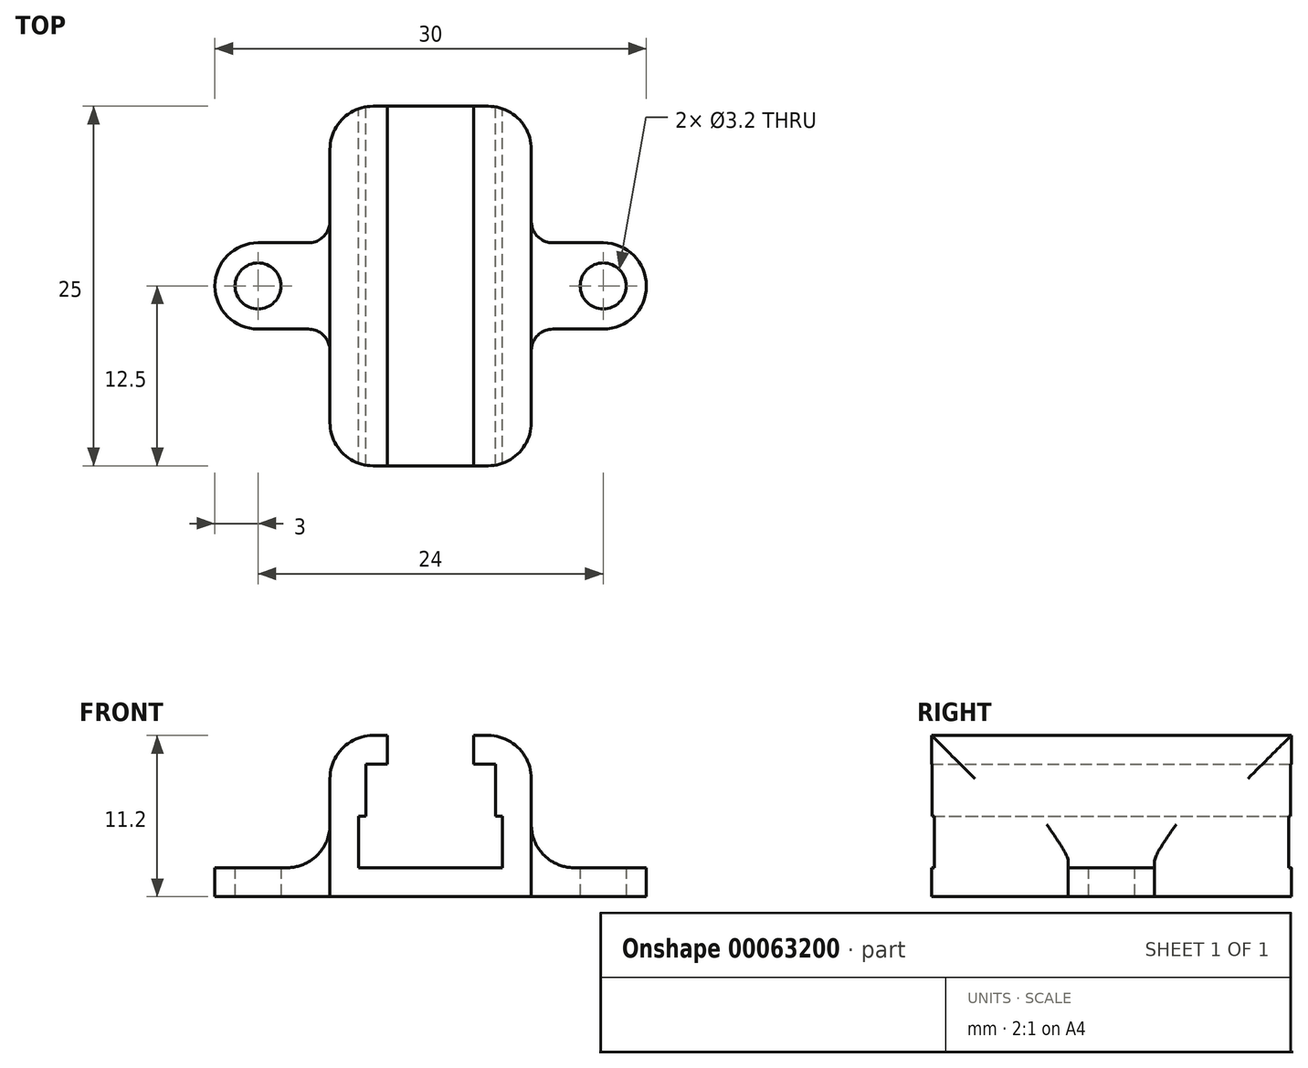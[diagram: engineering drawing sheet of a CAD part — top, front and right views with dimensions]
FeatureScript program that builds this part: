
annotation { "Feature Type Name" : "Feature", "Feature Type Description" : "" }
export const myFeature = defineFeature(function(context is Context, id is Id, definition is map)
    precondition{}
    {
        {
            var Q0;
            Q0=qCreatedBy(makeId("Front.planeOp"),FACE);
            var sketch = newSketch(context, id + "F0", { "sketchPlane" : qUnion([Q0])});
            skLineSegment(sketch, "E0", {"start": v(0, 0) * mm, "end": v(7, 0) * mm});
            skLineSegment(sketch, "E1", {"start": v(7, 0) * mm, "end": v(7, 11.2) * mm});
            skLineSegment(sketch, "E2", {"start": v(7, 11.2) * mm, "end": v(3, 11.2) * mm});
            skLineSegment(sketch, "E3", {"start": v(3, 11.2) * mm, "end": v(3, 9.2) * mm});
            skLineSegment(sketch, "E4", {"start": v(3, 9.2) * mm, "end": v(4.5, 9.2) * mm});
            skLineSegment(sketch, "E5", {"start": v(4.5, 9.2) * mm, "end": v(4.5, 5.6) * mm});
            skLineSegment(sketch, "E6", {"start": v(4.5, 5.6) * mm, "end": v(5, 5.6) * mm});
            skLineSegment(sketch, "E7", {"start": v(5, 5.6) * mm, "end": v(5, 2) * mm});
            skLineSegment(sketch, "E8", {"start": v(5, 2) * mm, "end": v(0, 2) * mm});
            skLineSegment(sketch, "E9", {"start": v(0, 2) * mm, "end": v(0, 0) * mm});
            skSolve(sketch);
        }
        {
            var Q0;
            Q0 = qSketchRegion(id + "F0", true);
            extrude(context, id + "F1", {"entities" : qUnion([Q0]), "depth" : 25 * mm});
        }
        {
            var Q0;
            Q0=qCreatedBy(makeId("Top.planeOp"),FACE);
            var sketch = newSketch(context, id + "F2", { "sketchPlane" : qUnion([Q0])});
            skLineSegment(sketch, "E10", {"start": v(0, 0) * mm, "end": v(0, -25) * mm, "construction": true});
            skLineSegment(sketch, "E11.bottom", {"start": v(8.5, -9.5) * mm, "end": v(15, -9.5) * mm});
            skLineSegment(sketch, "E11.top", {"start": v(8.5, -15.5) * mm, "end": v(15, -15.5) * mm});
            skLineSegment(sketch, "E11.left", {"start": v(0, -9.5) * mm, "end": v(0, -15.5) * mm});
            skLineSegment(sketch, "E11.right", {"start": v(15, -9.5) * mm, "end": v(15, -15.5) * mm});
            skLineSegment(sketch, "E12", {"start": v(15, -12.5) * mm, "end": v(0, -12.5) * mm, "construction": true});
            skCircle(sketch, "E13", {"center": v(12, -12.5) * mm, "radius": 1.6 * mm});
            skCircle(sketch, "E14", {"center": v(8.5, -8) * mm, "radius": 1.5 * mm, "construction": true});
            skLineSegment(sketch, "E15", {"start": v(8.5, -8) * mm, "end": v(8.5, -9.5) * mm, "construction": true});
            skLineSegment(sketch, "E16", {"start": v(8.5, -8) * mm, "end": v(7, -8) * mm, "construction": true});
            skArc(sketch, "E17", {"start": v(7, -8) * mm, "mid": v(7.44, -9.06) * mm, "end": v(8.5, -9.5) * mm});
            skLineSegment(sketch, "E18", {"start": v(7, -8) * mm, "end": v(0, -8) * mm});
            skLineSegment(sketch, "E19", {"start": v(0, -8) * mm, "end": v(0, -9.5) * mm});
            skLineSegment(sketch, "E20.MirrorCS", {"start": v(0, -17) * mm, "end": v(0, -15.5) * mm});
            skLineSegment(sketch, "E21.MirrorCS", {"start": v(7, -17) * mm, "end": v(0, -17) * mm});
            skArc(sketch, "E22.MirrorCS", {"start": v(7, -17) * mm, "mid": v(7.44, -15.94) * mm, "end": v(8.5, -15.5) * mm});
            skSolve(sketch);
        }
        {
            var Q0;
            Q0 = qSketchRegion(id + "F2", true);
            extrude(context, id + "F3", {"entities" : qUnion([Q0]), "operationType" : NewBodyOperationType.ADD, "depth" : 2 * mm});
        }
        {
            var Q0;
            Q0=makeQuery(id+"F3.boolean.opBoolean","INTERSECT",EDGE,{"derivedFrom":[makeQuery(id+"F1.opExtrude","SWEPT_FACE",FACE,{"disambiguationData":[OSD([sQuery(id+"F0.wireOp",EDGE,"E1")])]}),makeQuery(id+"F3.opExtrude","CAP_FACE",FACE,{"disambiguationData":[OSD([sQuery(id+"F2.wireOp",EDGE,"E11.bottom"),sQuery(id+"F2.wireOp",EDGE,"E11.top"),sQuery(id+"F2.wireOp",EDGE,"E11.left"),sQuery(id+"F2.wireOp",EDGE,"E11.right"),sQuery(id+"F2.wireOp",EDGE,"E13"),sQuery(id+"F2.wireOp",EDGE,"E17"),sQuery(id+"F2.wireOp",EDGE,"E18"),sQuery(id+"F2.wireOp",EDGE,"E19"),sQuery(id+"F2.wireOp",EDGE,"E20.MirrorCS"),sQuery(id+"F2.wireOp",EDGE,"E21.MirrorCS"),sQuery(id+"F2.wireOp",EDGE,"E22.MirrorCS")])],"isStart":false})]});
            var Q1;
            Q1=makeQuery(id+"F3.opExtrude","SWEPT_EDGE",EDGE,{"disambiguationData":[OSD([sQuery(id+"F2.wireOp",EDGE,"E11.top"),sQuery(id+"F2.wireOp",EDGE,"E11.right")])]});
            var Q2;
            Q2=makeQuery(id+"F3.opExtrude","SWEPT_EDGE",EDGE,{"disambiguationData":[OSD([sQuery(id+"F2.wireOp",EDGE,"E11.bottom"),sQuery(id+"F2.wireOp",EDGE,"E11.right")])]});
            var Q3;
            Q3=makeQuery(id+"F1.opExtrude","CAP_EDGE",EDGE,{"disambiguationData":[OSD([sQuery(id+"F0.wireOp",EDGE,"E1")])],"isStart":false});
            var Q4;
            Q4=makeQuery(id+"F1.opExtrude","CAP_EDGE",EDGE,{"disambiguationData":[OSD([sQuery(id+"F0.wireOp",EDGE,"E1")])],"isStart":true});
            var Q5;
            Q5=makeQuery(id+"F1.opExtrude","SWEPT_EDGE",EDGE,{"disambiguationData":[OSD([sQuery(id+"F0.wireOp",EDGE,"E1"),sQuery(id+"F0.wireOp",EDGE,"E2")])]});
            fillet(context, id + "F4", {"entities" : qUnion([Q0, Q1, Q2, Q3, Q4, Q5]), "radius" : 3 * mm, "tangentPropagation" : true, "allowEdgeOverflow" : false});
        }
        {
            var Q0;
            Q0=makeQuery(id+"F1.opExtrude","SWEPT_BODY",BODY,{"disambiguationData":[OSD([sQuery(id+"F0.wireOp",EDGE,"E0"),sQuery(id+"F0.wireOp",EDGE,"E1"),sQuery(id+"F0.wireOp",EDGE,"E2"),sQuery(id+"F0.wireOp",EDGE,"E3"),sQuery(id+"F0.wireOp",EDGE,"E4"),sQuery(id+"F0.wireOp",EDGE,"E5"),sQuery(id+"F0.wireOp",EDGE,"E6"),sQuery(id+"F0.wireOp",EDGE,"E7"),sQuery(id+"F0.wireOp",EDGE,"E8"),sQuery(id+"F0.wireOp",EDGE,"E9")])]});
            var Q1;
            Q1=makeQuery(id+"F1.opExtrude","SWEPT_FACE",FACE,{"disambiguationData":[OSD([sQuery(id+"F0.wireOp",EDGE,"E9")])]});
            mirror(context, id + "F5", {"operationType" : NewBodyOperationType.ADD, "entities" : qUnion([Q0]), "mirrorPlane" : qUnion([Q1])});
        }
    });
